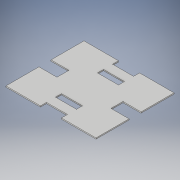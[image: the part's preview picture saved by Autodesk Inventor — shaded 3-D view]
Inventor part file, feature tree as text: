
AUTODESK INVENTOR PART (.ipt)
format: ipt  version: 2018 (Build 220112000, 112)  size: 134,144 bytes
history: native  units: in
note: dims shown in document units (in); Inventor stores cm internally (conversion verified against a paired STEP export)
features: extrude x1, sketch x1
ambient origin geometry x8: Origin, YZ Plane, XZ Plane, XY Plane, X Axis, Y Axis, Z Axis, Center Point
bodies: Body1 (feature_tree)
feature tree (2):
  extrude  "Extrusion3"  Depth=4.0in
  sketch  "Sketch1"  dims[d9=6.0in d10=4.0in d14=6.0in d15=4.0in d27=7.0in d29=7.0in d30=2.0in d31=2.0in d32=2.0in d33=3.0in d34=7.0in d35=2.0in d36=3.0in d37=7.0in d38=2.0in d39=0.375in d40=0.0in]
